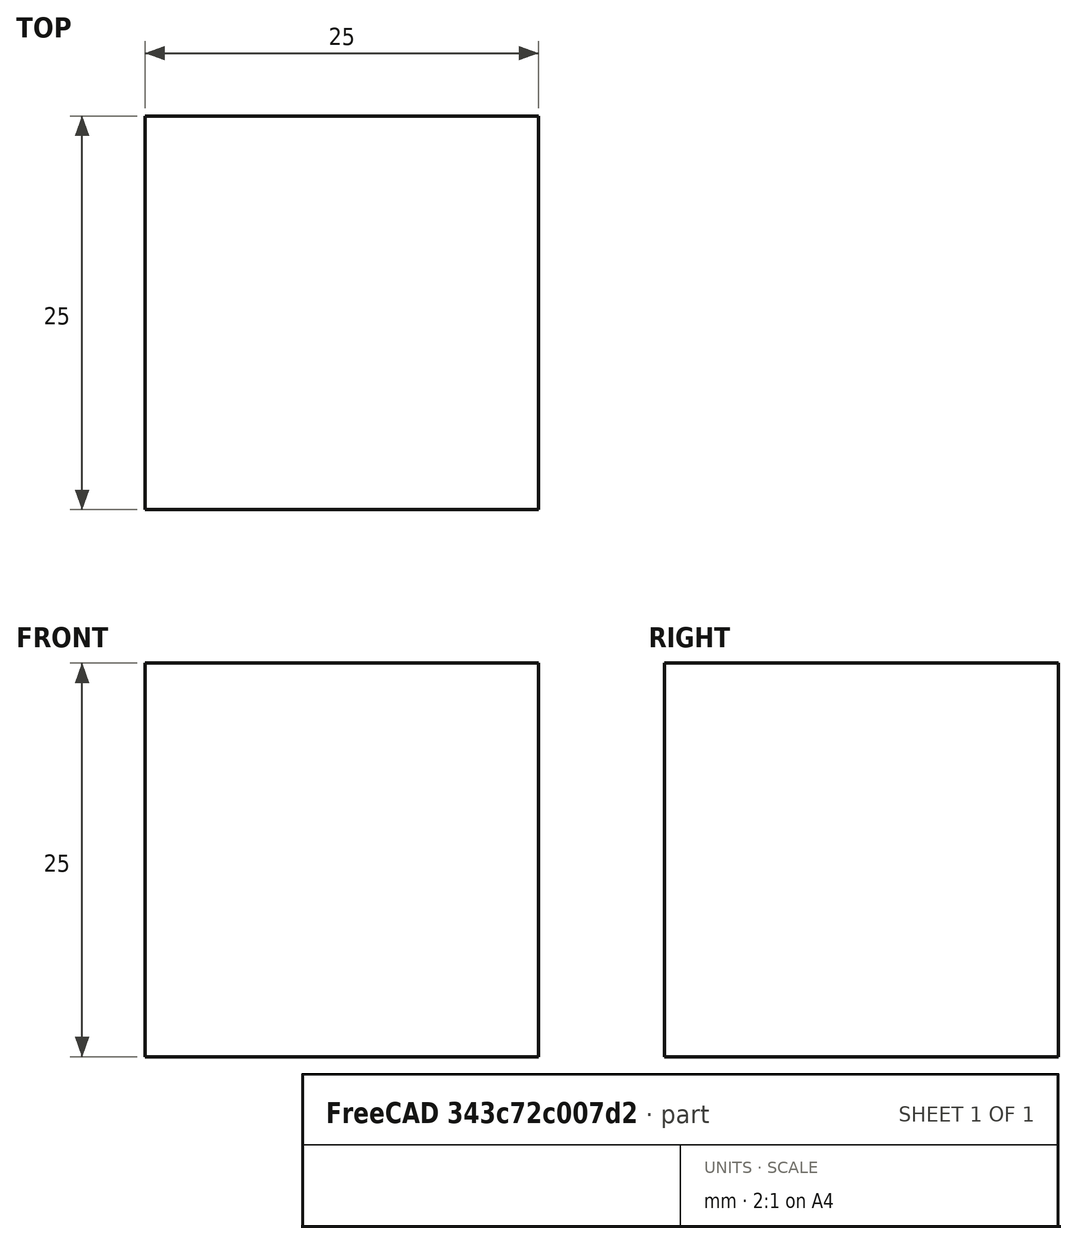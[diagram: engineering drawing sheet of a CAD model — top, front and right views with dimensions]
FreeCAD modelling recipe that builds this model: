
FCSTD DOCUMENT  (FreeCAD 0.19R24366 (Git))
Label: Part2Hollow
License: All rights reserved
LicenseURL: http://en.wikipedia.org/wiki/All_rights_reserved
objects: TechDraw::DrawViewDimension×2, Sketcher::SketchObject×1, PartDesign::Pad×1, PartDesign::Body×1, TechDraw::DrawSVGTemplate×1, TechDraw::DrawViewPart×1, TechDraw::DrawPage×1
note: 4 computed .brp shape members not serialized (recipe doc carries the construction recipe); baked Part::Feature solids carry a one-line shape summary decoded from their .brp

FEATURE [Sketcher::SketchObject] Sketch
  FullyConstrained = true
  MapMode = 5
  Placement = pos=(0,0,0) rot=(1,0,0;1.5708rad)
  Support = -> [XZ_Plane]
  sketch-geometry (4):
    g0: LineSegment StartX=-12.5 StartY=12.5 StartZ=0 EndX=12.5 EndY=12.5 EndZ=0
    g1: LineSegment StartX=12.5 StartY=12.5 StartZ=0 EndX=12.5 EndY=-12.5 EndZ=0
    g2: LineSegment StartX=12.5 StartY=-12.5 StartZ=0 EndX=-12.5 EndY=-12.5 EndZ=0
    g3: LineSegment StartX=-12.5 StartY=-12.5 StartZ=0 EndX=-12.5 EndY=12.5 EndZ=0
  constraints (12):
    c: Coincident(g0,g1)
    c: Coincident(g1,g2)
    c: Coincident(g2,g3)
    c: Coincident(g3,g0)
    c: Horizontal(g0)
    c: Horizontal(g2)
    c: Vertical(g1)
    c: Vertical(g3)
    c: DistanceX(g0,g0) = 25
    c: DistanceY(g1,g0) = 25
    c: DistanceY(g-1,g0) = 12.5
    c: DistanceX(g2,g-1) = 12.5
FEATURE [PartDesign::Pad] Pad
  Direction = (1,1,1)
  Length = 25
  Length2 = 100
  Placement = pos=(0,0,0) rot=(1,0,0;1.5708rad)
  Profile = -> Sketch
  Type = 0
FEATURE [PartDesign::Body] Body
  Group = -> [Sketch,Pad]
  Origin = -> Origin
  Tip = -> Pad
FEATURE [TechDraw::DrawSVGTemplate] Template
  EditableTexts = AUTHOR_NAME=Natan Hari Pamungkas; DN=Part - 02; DRAWING_TITLE=Part Besi Hollow - 02; FC-DATE=18/03/2022; FC-REV=REV A; FC-SC=3; FC-SH=X / Y; FC-SI=A4; FreeCAD_DRAWING=Jumlah item 2; PN=Hollow - 02; SI-1=Besi Hollow Ukuran 2.5 cm x 2.5 cm; SI-2=Ketebalan menyesuaikan
  Height = 297
  Orientation = 0
  Width = 210
FEATURE [TechDraw::DrawViewPart] View  label="Front"
  CoarseView = false
  Direction = (0,-1,0)
  Focus = 100
  HardHidden = false
  IsoCount = 0
  IsoHidden = false
  IsoVisible = false
  LockPosition = false
  Perspective = false
  Rotation = 0
  Scale = 3
  ScaleType = 0
  SeamHidden = false
  SeamVisible = true
  SmoothHidden = false
  SmoothVisible = true
  Source = -> [Body]
  X = 107.724
  XDirection = (1,0,0)
  Y = 171.653
FEATURE [TechDraw::DrawViewDimension] Dimension
  Arbitrary = false
  ArbitraryTolerances = false
  EqualTolerance = true
  FormatSpec = %.2f
  FormatSpecOverTolerance = %+.2f
  FormatSpecUnderTolerance = %+.2f
  Inverted = false
  LockPosition = false
  MeasureType = 1
  OverTolerance = 0
  References2D = -> [View]
  Rotation = 0
  ScaleType = 0
  TheoreticalExact = false
  Type = 1
  UnderTolerance = 0
  X = -0.54477
  Y = 57.3841
FEATURE [TechDraw::DrawViewDimension] Dimension001
  Arbitrary = false
  ArbitraryTolerances = false
  EqualTolerance = true
  FormatSpec = %.2f
  FormatSpecOverTolerance = %+.2f
  FormatSpecUnderTolerance = %+.2f
  Inverted = false
  LockPosition = false
  MeasureType = 1
  OverTolerance = 0
  References2D = -> [View]
  Rotation = 0
  ScaleType = 0
  TheoreticalExact = false
  Type = 2
  UnderTolerance = 0
  X = 56.567
  Y = -0.54477
FEATURE [TechDraw::DrawPage] Page
  KeepUpdated = true
  NextBalloonIndex = 1
  ProjectionType = 0
  Template = -> Template
  Views = -> [View,Dimension,Dimension001]
